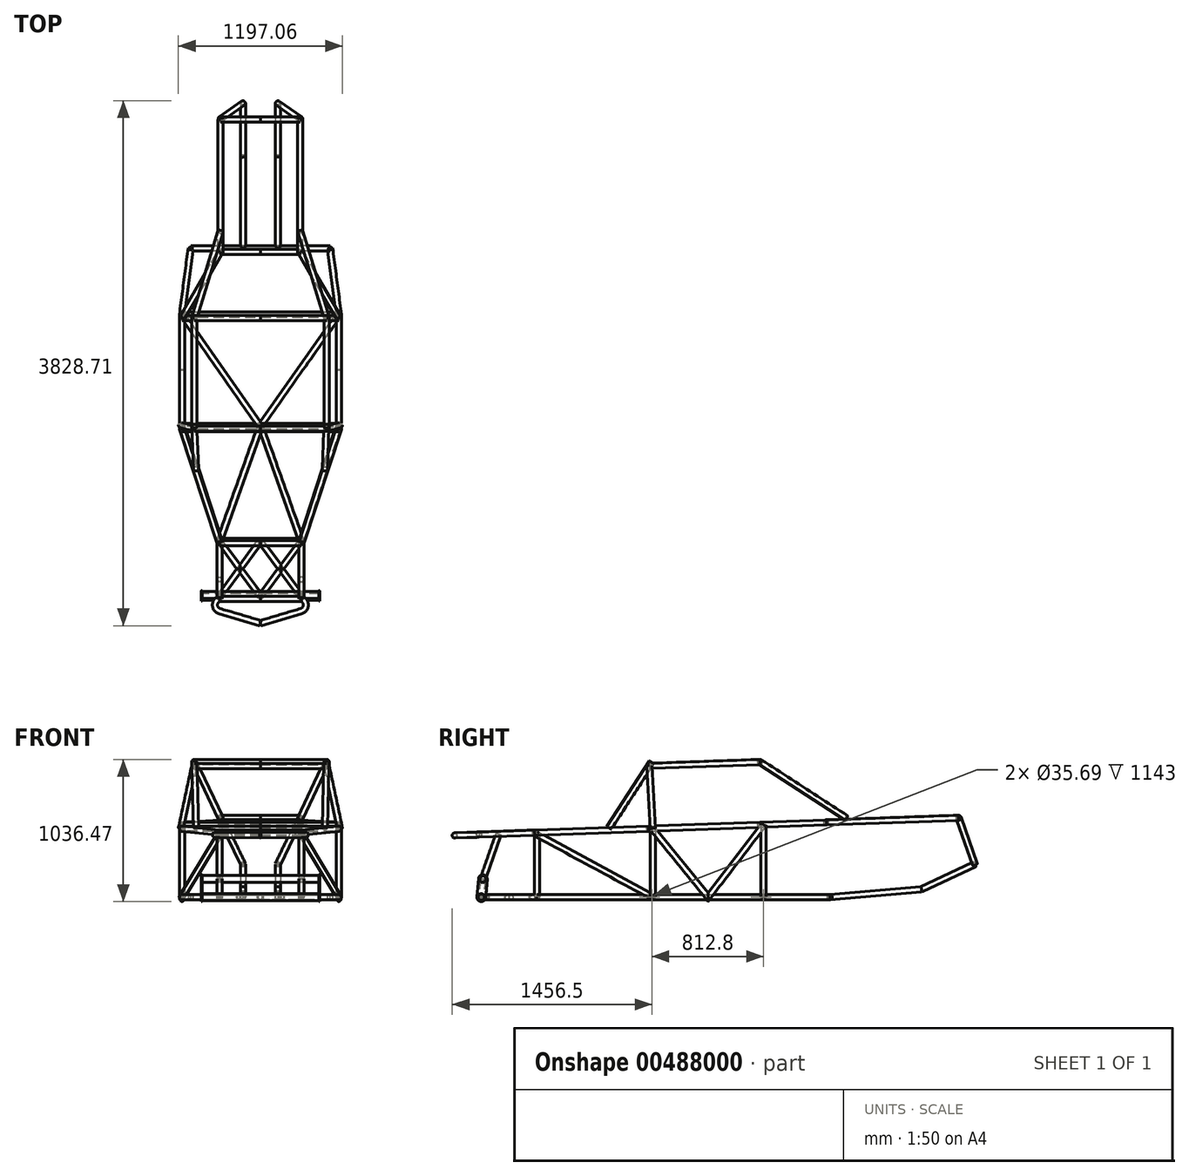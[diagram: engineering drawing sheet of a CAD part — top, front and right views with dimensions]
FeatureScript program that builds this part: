
annotation { "Feature Type Name" : "Feature", "Feature Type Description" : "" }
export const myFeature = defineFeature(function(context is Context, id is Id, definition is map)
    precondition{}
    {
        {
            var Q0;
            Q0=qCreatedBy(makeId("Top.planeOp"),FACE);
            var sketch = newSketch(context, id + "F0", { "sketchPlane" : qUnion([Q0])});
            skLineSegment(sketch, "E0", {"start": v(0, 0) * mm, "end": v(298.45, 0) * mm});
            skLineSegment(sketch, "E1", {"start": v(298.45, 0) * mm, "end": v(-298.45, 0) * mm});
            skLineSegment(sketch, "E2", {"start": v(-298.45, 0) * mm, "end": v(-298.45, 406.4) * mm});
            skLineSegment(sketch, "E3", {"start": v(298.45, 0) * mm, "end": v(298.45, 406.4) * mm});
            skLineSegment(sketch, "E4", {"start": v(-298.45, 406.4) * mm, "end": v(298.45, 406.4) * mm});
            skLineSegment(sketch, "E5", {"start": v(-571.5, 1244.6) * mm, "end": v(-298.45, 406.4) * mm});
            skLineSegment(sketch, "E6", {"start": v(298.45, 406.4) * mm, "end": v(571.5, 1244.6) * mm});
            skLineSegment(sketch, "E7", {"start": v(-571.5, 1244.6) * mm, "end": v(571.5, 1244.6) * mm});
            skLineSegment(sketch, "E8", {"start": v(-571.5, 1244.6) * mm, "end": v(-571.5, 2057.4) * mm});
            skLineSegment(sketch, "E9", {"start": v(571.5, 1244.6) * mm, "end": v(571.5, 2057.4) * mm});
            skLineSegment(sketch, "E10", {"start": v(508, 2540) * mm, "end": v(571.5, 2057.4) * mm});
            skLineSegment(sketch, "E11", {"start": v(-571.5, 2057.4) * mm, "end": v(-508, 2540) * mm});
            skLineSegment(sketch, "E12", {"start": v(-571.5, 2057.4) * mm, "end": v(571.5, 2057.4) * mm});
            skLineSegment(sketch, "E13", {"start": v(-508, 2540) * mm, "end": v(508, 2540) * mm});
            skLineSegment(sketch, "E14", {"start": v(0, 0) * mm, "end": v(0, 2540) * mm});
            skLineSegment(sketch, "E15", {"start": v(-298.45, 406.4) * mm, "end": v(0, 0) * mm});
            skLineSegment(sketch, "E16", {"start": v(0, 406.4) * mm, "end": v(-298.45, 0) * mm});
            skLineSegment(sketch, "E17", {"start": v(298.45, 0) * mm, "end": v(0, 406.4) * mm});
            skLineSegment(sketch, "E18", {"start": v(0, 0) * mm, "end": v(298.45, 406.4) * mm});
            skLineSegment(sketch, "E19", {"start": v(-298.45, 406.4) * mm, "end": v(0, 1244.6) * mm});
            skLineSegment(sketch, "E20", {"start": v(0, 1244.6) * mm, "end": v(298.45, 406.4) * mm});
            skLineSegment(sketch, "E21", {"start": v(0, 1244.6) * mm, "end": v(-571.5, 2057.4) * mm});
            skLineSegment(sketch, "E22", {"start": v(0, 1244.6) * mm, "end": v(571.5, 2057.4) * mm});
            skSolve(sketch);
        }
        {
            var Q0;
            Q0=qCreatedBy(makeId("Top.planeOp"),FACE);
            cPlane(context, id + "F1", {"entities" : qUnion([Q0]), "cplaneType" : CPlaneType.OFFSET, "offset" : 457.2 * mm, "width" : 152.4 * mm, "height" : 152.4 * mm});
        }
        {
            var Q0;
            Q0=qCreatedBy(id+"F1.planeOp",FACE);
            var sketch = newSketch(context, id + "F2", { "sketchPlane" : qUnion([Q0])});
            skLineSegment(sketch, "E23", {"start": v(0, 0) * mm, "end": v(298.45, 0) * mm});
            skLineSegment(sketch, "E24", {"start": v(298.45, 0) * mm, "end": v(298.45, 406.4) * mm});
            skLineSegment(sketch, "E25", {"start": v(298.45, 406.4) * mm, "end": v(571.34, 1239.13) * mm});
            skLineSegment(sketch, "E26", {"start": v(571.34, 1239.13) * mm, "end": v(571.34, 2051.93) * mm});
            skLineSegment(sketch, "E27", {"start": v(0, 0) * mm, "end": v(-298.45, 0) * mm});
            skLineSegment(sketch, "E28", {"start": v(-298.45, 0) * mm, "end": v(-298.45, 406.4) * mm});
            skLineSegment(sketch, "E29", {"start": v(-298.45, 406.4) * mm, "end": v(-570.8, 1239.3) * mm});
            skLineSegment(sketch, "E30", {"start": v(-570.8, 1239.3) * mm, "end": v(-570.8, 2052.1) * mm});
            skLineSegment(sketch, "E31", {"start": v(-298.45, 406.4) * mm, "end": v(298.45, 406.4) * mm});
            skLineSegment(sketch, "E32", {"start": v(571.34, 1239.13) * mm, "end": v(-570.8, 1239.3) * mm});
            skLineSegment(sketch, "E33", {"start": v(571.34, 2051.93) * mm, "end": v(-570.8, 2052.1) * mm});
            skLineSegment(sketch, "E34", {"start": v(310.25, 2534.7) * mm, "end": v(571.34, 2051.93) * mm});
            skLineSegment(sketch, "E35", {"start": v(-316.8, 2534.7) * mm, "end": v(-570.8, 2052.1) * mm});
            skLineSegment(sketch, "E36", {"start": v(-316.8, 2534.7) * mm, "end": v(310.25, 2534.7) * mm});
            skLineSegment(sketch, "E37", {"start": v(-316.8, 2534.7) * mm, "end": v(-316.8, 3499.9) * mm});
            skLineSegment(sketch, "E38", {"start": v(-316.8, 3499.9) * mm, "end": v(310.25, 3499.9) * mm});
            skLineSegment(sketch, "E39", {"start": v(310.25, 3499.9) * mm, "end": v(310.25, 2534.7) * mm});
            skLineSegment(sketch, "E40", {"start": v(-570.8, 1239.3) * mm, "end": v(298.45, 406.4) * mm});
            skLineSegment(sketch, "E41", {"start": v(571.34, 1239.13) * mm, "end": v(-298.45, 406.4) * mm});
            skSolve(sketch);
        }
        {
            var Q0;
            Q0=qCreatedBy(makeId("Front.planeOp"),FACE);
            var sketch = newSketch(context, id + "F3", { "sketchPlane" : qUnion([Q0])});
            skCircle(sketch, "E42", {"center": v(-298.45, 0) * mm, "radius": 19.05 * mm});
            skCircle(sketch, "E43", {"center": v(-298.45, 0) * mm, "radius": 17.84 * mm});
            skSolve(sketch);
        }
        {
            var Q0;
            Q0=makeQuery(id+"F3.imprint","IMPRINT",FACE,{"disambiguationData":[TD([[makeQuery(id+"F3.imprint","IMPRINT",EDGE,{"derivedFrom":sQuery(id+"F3.wireOp",EDGE,"E42")}),1.0]])]});
            var Q1;
            Q1=sQuery(id+"F0.wireOp",EDGE,"E2");
            var Q2;
            Q2=sQuery(id+"F0.wireOp",EDGE,"E5");
            var Q3;
            Q3=sQuery(id+"F0.wireOp",EDGE,"E8");
            var Q4;
            Q4=sQuery(id+"F0.wireOp",EDGE,"E11");
            sweep(context, id + "F4", {"profiles" : qUnion([Q0]), "path" : qUnion([Q1, Q2, Q3, Q4])});
        }
        {
            var Q0;
            Q0=sQuery(id+"F0.wireOp",EDGE,"E16");
            var Q1;
            Q1=sQuery(id+"F0.wireOp",VERTEX,"E16.end");
            cPlane(context, id + "F5", {"entities" : qUnion([Q0, Q1]), "cplaneType" : CPlaneType.LINE_POINT, "offset" : 25.4 * mm, "width" : 152.4 * mm, "height" : 152.4 * mm});
        }
        {
            var Q0;
            Q0=qCreatedBy(id+"F5.planeOp",FACE);
            var sketch = newSketch(context, id + "F6", { "sketchPlane" : qUnion([Q0])});
            skCircle(sketch, "E44", {"center": v(-240.55, 0) * mm, "radius": 19.05 * mm});
            skCircle(sketch, "E45", {"center": v(-240.55, 0) * mm, "radius": 17.84 * mm});
            skSolve(sketch);
        }
        {
            var Q0;
            Q0=makeQuery(id+"F6.imprint","IMPRINT",FACE,{"disambiguationData":[TD([[makeQuery(id+"F6.imprint","IMPRINT",EDGE,{"derivedFrom":sQuery(id+"F6.wireOp",EDGE,"E44")}),1.0]])]});
            var Q1;
            Q1=sQuery(id+"F0.wireOp",EDGE,"E16");
            sweep(context, id + "F7", {"operationType" : NewBodyOperationType.ADD, "profiles" : qUnion([Q0]), "path" : qUnion([Q1])});
        }
        {
            var Q0;
            Q0=sQuery(id+"F0.wireOp",VERTEX,"E15.end");
            var Q1;
            Q1=sQuery(id+"F0.wireOp",EDGE,"E15");
            cPlane(context, id + "F8", {"entities" : qUnion([Q0, Q1]), "cplaneType" : CPlaneType.LINE_POINT, "offset" : 25.4 * mm, "width" : 152.4 * mm, "height" : 152.4 * mm});
        }
        {
            var Q0;
            Q0=qCreatedBy(id+"F8.planeOp",FACE);
            var sketch = newSketch(context, id + "F9", { "sketchPlane" : qUnion([Q0])});
            skCircle(sketch, "E46", {"center": v(0, 0) * mm, "radius": 19.05 * mm});
            skCircle(sketch, "E47", {"center": v(0, 0) * mm, "radius": 17.84 * mm});
            skSolve(sketch);
        }
        {
            var Q0;
            Q0=makeQuery(id+"F9.imprint","IMPRINT",FACE,{"disambiguationData":[TD([[makeQuery(id+"F9.imprint","IMPRINT",EDGE,{"derivedFrom":sQuery(id+"F9.wireOp",EDGE,"E46")}),1.0]])]});
            var Q1;
            Q1=sQuery(id+"F0.wireOp",EDGE,"E15");
            sweep(context, id + "F10", {"operationType" : NewBodyOperationType.ADD, "profiles" : qUnion([Q0]), "path" : qUnion([Q1])});
        }
        {
            var Q0;
            Q0=makeQuery(id+"F4.opSweep","SWEPT_BODY",BODY,{"disambiguationData":[OSD([sQuery(id+"F0.wireOp",EDGE,"E11"),sQuery(id+"F3.wireOp",EDGE,"E42"),sQuery(id+"F3.wireOp",EDGE,"E43")])]});
            var Q1;
            Q1=qCreatedBy(makeId("Right.planeOp"),FACE);
            mirror(context, id + "F11", {"entities" : qUnion([Q0]), "mirrorPlane" : qUnion([Q1])});
        }
        {
            var Q0;
            Q0=sQuery(id+"F0.wireOp",VERTEX,"E19.start");
            var Q1;
            Q1=sQuery(id+"F0.wireOp",EDGE,"E4");
            cPlane(context, id + "F12", {"entities" : qUnion([Q0, Q1]), "cplaneType" : CPlaneType.LINE_POINT, "offset" : 25.4 * mm, "width" : 152.4 * mm, "height" : 152.4 * mm});
        }
        {
            var Q0;
            Q0=qCreatedBy(id+"F12.planeOp",FACE);
            var sketch = newSketch(context, id + "F13", { "sketchPlane" : qUnion([Q0])});
            skCircle(sketch, "E48", {"center": v(406.4, 0) * mm, "radius": 19.05 * mm});
            skCircle(sketch, "E49", {"center": v(406.4, 0) * mm, "radius": 17.84 * mm});
            skSolve(sketch);
        }
        {
            var Q0;
            Q0 = qSketchRegion(id + "F13", true);
            var Q1;
            Q1=sQuery(id+"F0.wireOp",EDGE,"E4");
            sweep(context, id + "F14", {"profiles" : qUnion([Q0]), "path" : qUnion([Q1])});
        }
        {
            var Q0;
            Q0=sQuery(id+"F0.wireOp",VERTEX,"E5.start");
            var Q1;
            Q1=sQuery(id+"F0.wireOp",EDGE,"E7");
            cPlane(context, id + "F15", {"entities" : qUnion([Q0, Q1]), "cplaneType" : CPlaneType.LINE_POINT, "offset" : 25.4 * mm, "width" : 152.4 * mm, "height" : 152.4 * mm});
        }
        {
            var Q0;
            Q0=qCreatedBy(id+"F15.planeOp",FACE);
            var sketch = newSketch(context, id + "F16", { "sketchPlane" : qUnion([Q0])});
            skCircle(sketch, "E50", {"center": v(1244.6, 0) * mm, "radius": 19.05 * mm});
            skCircle(sketch, "E51", {"center": v(1244.6, 0) * mm, "radius": 17.84 * mm});
            skCircle(sketch, "E52", {"center": v(2057.4, 0) * mm, "radius": 19.05 * mm});
            skCircle(sketch, "E53", {"center": v(2057.4, 0) * mm, "radius": 17.84 * mm});
            skSolve(sketch);
        }
        {
            var Q0;
            Q0 = qSketchRegion(id + "F16", true);
            var Q1;
            Q1=sQuery(id+"F0.wireOp",EDGE,"E7");
            sweep(context, id + "F17", {"profiles" : qUnion([Q0]), "path" : qUnion([Q1])});
        }
        {
            var Q0;
            Q0=sQuery(id+"F0.wireOp",VERTEX,"E11.end");
            var Q1;
            Q1=sQuery(id+"F0.wireOp",EDGE,"E13");
            cPlane(context, id + "F18", {"entities" : qUnion([Q0, Q1]), "cplaneType" : CPlaneType.LINE_POINT, "offset" : 25.4 * mm, "width" : 152.4 * mm, "height" : 152.4 * mm});
        }
        {
            var Q0;
            Q0=qCreatedBy(id+"F18.planeOp",FACE);
            var sketch = newSketch(context, id + "F19", { "sketchPlane" : qUnion([Q0])});
            skCircle(sketch, "E54", {"center": v(2540, 0) * mm, "radius": 19.05 * mm});
            skCircle(sketch, "E55", {"center": v(2540, 0) * mm, "radius": 17.84 * mm});
            skSolve(sketch);
        }
        {
            var Q0;
            Q0 = qSketchRegion(id + "F19", true);
            var Q1;
            Q1=sQuery(id+"F0.wireOp",EDGE,"E13");
            sweep(context, id + "F20", {"profiles" : qUnion([Q0]), "path" : qUnion([Q1])});
        }
        {
            var Q0;
            Q0=sQuery(id+"F0.wireOp",VERTEX,"E19.start");
            var Q1;
            Q1=sQuery(id+"F0.wireOp",EDGE,"E19");
            cPlane(context, id + "F21", {"entities" : qUnion([Q0, Q1]), "cplaneType" : CPlaneType.LINE_POINT, "offset" : 25.4 * mm, "width" : 152.4 * mm, "height" : 152.4 * mm});
        }
        {
            var Q0;
            Q0=qCreatedBy(id+"F21.planeOp",FACE);
            var sketch = newSketch(context, id + "F22", { "sketchPlane" : qUnion([Q0])});
            skCircle(sketch, "E56", {"center": v(417.48, 0) * mm, "radius": 19.05 * mm});
            skCircle(sketch, "E57", {"center": v(417.48, 0) * mm, "radius": 17.84 * mm});
            skSolve(sketch);
        }
        {
            var Q0;
            Q0 = qSketchRegion(id + "F22", true);
            var Q1;
            Q1=sQuery(id+"F0.wireOp",EDGE,"E19");
            var Q2;
            Q2=sQuery(id+"F0.wireOp",EDGE,"E21");
            sweep(context, id + "F23", {"profiles" : qUnion([Q0]), "path" : qUnion([Q1, Q2])});
        }
        {
            var Q0;
            Q0=makeQuery(id+"F23.opSweep","SWEPT_BODY",BODY,{"disambiguationData":[OSD([sQuery(id+"F0.wireOp",EDGE,"E21"),sQuery(id+"F22.wireOp",EDGE,"E56"),sQuery(id+"F22.wireOp",EDGE,"E57")])]});
            var Q1;
            Q1=qCreatedBy(makeId("Right.planeOp"),FACE);
            mirror(context, id + "F24", {"entities" : qUnion([Q0]), "mirrorPlane" : qUnion([Q1])});
        }
        {
            var Q0;
            Q0=qCreatedBy(id+"F1.planeOp",FACE);
            var Q1;
            Q1=sQuery(id+"F2.wireOp",EDGE,"E27");
            cPlane(context, id + "F25", {"entities" : qUnion([Q0, Q1]), "cplaneType" : CPlaneType.LINE_ANGLE, "offset" : 25.4 * mm, "angle" : 178 * degree, "width" : 152.4 * mm, "height" : 152.4 * mm});
        }
        {
            var Q0;
            Q0=qCreatedBy(id+"F25.planeOp",FACE);
            var sketch = newSketch(context, id + "F26", { "sketchPlane" : qUnion([Q0])});
            skLineSegment(sketch, "E58", {"start": v(0, 0) * mm, "end": v(298.45, 0) * mm});
            skLineSegment(sketch, "E59", {"start": v(298.45, 0) * mm, "end": v(298.45, 407.92) * mm});
            skLineSegment(sketch, "E60", {"start": v(571.5, 1239.87) * mm, "end": v(298.45, 407.92) * mm});
            skLineSegment(sketch, "E61", {"start": v(571.5, 1239.87) * mm, "end": v(571.5, 2049.6) * mm});
            skLineSegment(sketch, "E62", {"start": v(298.45, 407.92) * mm, "end": v(0, 407.92) * mm});
            skLineSegment(sketch, "E63", {"start": v(571.5, 1239.87) * mm, "end": v(0, 1239.87) * mm});
            skLineSegment(sketch, "E64", {"start": v(571.5, 2049.6) * mm, "end": v(0, 2049.6) * mm});
            skLineSegment(sketch, "E65", {"start": v(291.24, 2531.52) * mm, "end": v(571.5, 2049.6) * mm});
            skLineSegment(sketch, "E66", {"start": v(291.24, 2531.52) * mm, "end": v(291.24, 3496.72) * mm});
            skLineSegment(sketch, "E67", {"start": v(291.24, 2531.52) * mm, "end": v(0, 2531.52) * mm});
            skLineSegment(sketch, "E68", {"start": v(291.24, 3496.72) * mm, "end": v(0, 3496.72) * mm});
            skSolve(sketch);
        }
        {
            var Q0;
            Q0=sQuery(id+"F26.wireOp",VERTEX,"E58.start");
            var Q1;
            Q1=sQuery(id+"F26.wireOp",EDGE,"E58");
            cPlane(context, id + "F27", {"entities" : qUnion([Q0, Q1]), "cplaneType" : CPlaneType.LINE_POINT, "offset" : 25.4 * mm, "width" : 152.4 * mm, "height" : 152.4 * mm});
        }
        {
            var Q0;
            Q0=qCreatedBy(id+"F27.planeOp",FACE);
            var sketch = newSketch(context, id + "F28", { "sketchPlane" : qUnion([Q0])});
            skCircle(sketch, "E69", {"center": v(-15.95, 456.64) * mm, "radius": 19.05 * mm});
            skCircle(sketch, "E70", {"center": v(-15.95, 456.64) * mm, "radius": 17.84 * mm});
            skCircle(sketch, "E71", {"center": v(391.73, 470.88) * mm, "radius": 19.05 * mm});
            skCircle(sketch, "E72", {"center": v(391.73, 470.88) * mm, "radius": 17.84 * mm});
            skSolve(sketch);
        }
        {
            var Q0;
            Q0 = qSketchRegion(id + "F28", true);
            var Q1;
            Q1=sQuery(id+"F26.wireOp",EDGE,"E58");
            sweep(context, id + "F29", {"profiles" : qUnion([Q0]), "path" : qUnion([Q1])});
        }
        {
            var Q0;
            Q0=sQuery(id+"F26.wireOp",VERTEX,"E63.end");
            var Q1;
            Q1=sQuery(id+"F26.wireOp",EDGE,"E63");
            cPlane(context, id + "F30", {"entities" : qUnion([Q0, Q1]), "cplaneType" : CPlaneType.LINE_POINT, "offset" : 25.4 * mm, "width" : 152.4 * mm, "height" : 152.4 * mm});
        }
        {
            var Q0;
            Q0=qCreatedBy(id+"F30.planeOp",FACE);
            var sketch = newSketch(context, id + "F31", { "sketchPlane" : qUnion([Q0])});
            skCircle(sketch, "E73", {"center": v(-1223.17, 499.91) * mm, "radius": 19.05 * mm});
            skCircle(sketch, "E74", {"center": v(-1223.17, 499.91) * mm, "radius": 17.84 * mm});
            skCircle(sketch, "E75", {"center": v(-2032.4, 528.17) * mm, "radius": 19.05 * mm});
            skCircle(sketch, "E76", {"center": v(-2032.4, 528.17) * mm, "radius": 17.84 * mm});
            skSolve(sketch);
        }
        {
            var Q0;
            Q0 = qSketchRegion(id + "F31", true);
            var Q1;
            Q1=sQuery(id+"F26.wireOp",EDGE,"E63");
            sweep(context, id + "F32", {"profiles" : qUnion([Q0]), "path" : qUnion([Q1])});
        }
        {
            var Q0;
            Q0=sQuery(id+"F26.wireOp",VERTEX,"E67.end");
            var Q1;
            Q1=sQuery(id+"F26.wireOp",EDGE,"E67");
            cPlane(context, id + "F33", {"entities" : qUnion([Q0, Q1]), "cplaneType" : CPlaneType.LINE_POINT, "offset" : 25.4 * mm, "width" : 152.4 * mm, "height" : 152.4 * mm});
        }
        {
            var Q0;
            Q0=qCreatedBy(id+"F33.planeOp",FACE);
            var sketch = newSketch(context, id + "F34", { "sketchPlane" : qUnion([Q0])});
            skCircle(sketch, "E77", {"center": v(-2514.04, 545) * mm, "radius": 19.05 * mm});
            skCircle(sketch, "E78", {"center": v(-2514.04, 545) * mm, "radius": 17.84 * mm});
            skCircle(sketch, "E79", {"center": v(-3478.65, 578.68) * mm, "radius": 19.05 * mm});
            skCircle(sketch, "E80", {"center": v(-3478.65, 578.68) * mm, "radius": 17.84 * mm});
            skSolve(sketch);
        }
        {
            var Q0;
            Q0 = qSketchRegion(id + "F34", true);
            var Q1;
            Q1=sQuery(id+"F26.wireOp",EDGE,"E67");
            sweep(context, id + "F35", {"profiles" : qUnion([Q0]), "path" : qUnion([Q1])});
        }
        {
            var Q0;
            Q0=sQuery(id+"F26.wireOp",VERTEX,"E59.start");
            var Q1;
            Q1=sQuery(id+"F26.wireOp",EDGE,"E59");
            cPlane(context, id + "F36", {"entities" : qUnion([Q0, Q1]), "cplaneType" : CPlaneType.LINE_POINT, "offset" : 25.4 * mm, "width" : 152.4 * mm, "height" : 152.4 * mm});
        }
        {
            var Q0;
            Q0=qCreatedBy(id+"F36.planeOp",FACE);
            var sketch = newSketch(context, id + "F37", { "sketchPlane" : qUnion([Q0])});
            skCircle(sketch, "E81", {"center": v(-298.45, 456.92) * mm, "radius": 19.05 * mm});
            skCircle(sketch, "E82", {"center": v(-298.45, 456.92) * mm, "radius": 17.84 * mm});
            skSolve(sketch);
        }
        {
            var Q0;
            Q0 = qSketchRegion(id + "F37", true);
            var Q1;
            Q1=sQuery(id+"F26.wireOp",EDGE,"E59");
            var Q2;
            Q2=sQuery(id+"F26.wireOp",EDGE,"E60");
            var Q3;
            Q3=sQuery(id+"F26.wireOp",EDGE,"E61");
            var Q4;
            Q4=sQuery(id+"F26.wireOp",EDGE,"E65");
            var Q5;
            Q5=sQuery(id+"F26.wireOp",EDGE,"E66");
            sweep(context, id + "F38", {"profiles" : qUnion([Q0]), "path" : qUnion([Q1, Q2, Q3, Q4, Q5])});
        }
        {
            var Q0;
            Q0=makeQuery(id+"F29.opSweep","SWEPT_BODY",BODY,{"disambiguationData":[OSD([sQuery(id+"F26.wireOp",EDGE,"E58"),sQuery(id+"F28.wireOp",EDGE,"E69"),sQuery(id+"F28.wireOp",EDGE,"E70")])]});
            var Q1;
            Q1=makeQuery(id+"F29.opSweep","SWEPT_BODY",BODY,{"disambiguationData":[OSD([sQuery(id+"F26.wireOp",EDGE,"E58"),sQuery(id+"F28.wireOp",EDGE,"E71"),sQuery(id+"F28.wireOp",EDGE,"E72")])]});
            var Q2;
            Q2=makeQuery(id+"F32.opSweep","SWEPT_BODY",BODY,{"disambiguationData":[OSD([sQuery(id+"F26.wireOp",EDGE,"E63"),sQuery(id+"F31.wireOp",EDGE,"E73"),sQuery(id+"F31.wireOp",EDGE,"E74")])]});
            var Q3;
            Q3=makeQuery(id+"F32.opSweep","SWEPT_BODY",BODY,{"disambiguationData":[OSD([sQuery(id+"F26.wireOp",EDGE,"E63"),sQuery(id+"F31.wireOp",EDGE,"E75"),sQuery(id+"F31.wireOp",EDGE,"E76")])]});
            var Q4;
            Q4=makeQuery(id+"F35.opSweep","SWEPT_BODY",BODY,{"disambiguationData":[OSD([sQuery(id+"F26.wireOp",EDGE,"E67"),sQuery(id+"F34.wireOp",EDGE,"E77"),sQuery(id+"F34.wireOp",EDGE,"E78")])]});
            var Q5;
            Q5=makeQuery(id+"F35.opSweep","SWEPT_BODY",BODY,{"disambiguationData":[OSD([sQuery(id+"F26.wireOp",EDGE,"E67"),sQuery(id+"F34.wireOp",EDGE,"E79"),sQuery(id+"F34.wireOp",EDGE,"E80")])]});
            var Q6;
            Q6=makeQuery(id+"F38.opSweep","SWEPT_BODY",BODY,{"disambiguationData":[OSD([sQuery(id+"F26.wireOp",EDGE,"E66"),sQuery(id+"F37.wireOp",EDGE,"E81"),sQuery(id+"F37.wireOp",EDGE,"E82")])]});
            var Q7;
            Q7=qCreatedBy(id+"F27.planeOp",FACE);
            mirror(context, id + "F39", {"entities" : qUnion([Q0, Q1, Q2, Q3, Q4, Q5, Q6]), "mirrorPlane" : qUnion([Q7])});
        }
        {
            var Q0;
            Q0=qCreatedBy(id+"F15.planeOp",FACE);
            var sketch = newSketch(context, id + "F40", { "sketchPlane" : qUnion([Q0])});
            skLineSegment(sketch, "E83", {"start": v(1251.69, 0) * mm, "end": v(1251.69, 499.7) * mm});
            skLineSegment(sketch, "E84", {"start": v(2058.56, 0) * mm, "end": v(2058.56, 528.86) * mm});
            skSolve(sketch);
        }
        {
            var Q0;
            Q0=sQuery(id+"F40.wireOp",EDGE,"E84");
            var Q1;
            Q1=sQuery(id+"F40.wireOp",VERTEX,"E84.end");
            cPlane(context, id + "F41", {"entities" : qUnion([Q0, Q1]), "cplaneType" : CPlaneType.LINE_POINT, "offset" : 25.4 * mm, "width" : 152.4 * mm, "height" : 152.4 * mm});
        }
        {
            var Q0;
            Q0=qCreatedBy(id+"F41.planeOp",FACE);
            var sketch = newSketch(context, id + "F42", { "sketchPlane" : qUnion([Q0])});
            skCircle(sketch, "E85", {"center": v(-571.5, 2058.56) * mm, "radius": 19.05 * mm});
            skCircle(sketch, "E86", {"center": v(-571.5, 2058.56) * mm, "radius": 17.84 * mm});
            skSolve(sketch);
        }
        {
            var Q0;
            Q0 = qSketchRegion(id + "F42", true);
            var Q1;
            Q1=sQuery(id+"F40.wireOp",EDGE,"E84");
            sweep(context, id + "F43", {"profiles" : qUnion([Q0]), "path" : qUnion([Q1])});
        }
        {
            var Q0;
            Q0=sQuery(id+"F40.wireOp",VERTEX,"E83.end");
            var Q1;
            Q1=sQuery(id+"F40.wireOp",EDGE,"E83");
            cPlane(context, id + "F44", {"entities" : qUnion([Q0, Q1]), "cplaneType" : CPlaneType.LINE_POINT, "offset" : 25.4 * mm, "width" : 152.4 * mm, "height" : 152.4 * mm});
        }
        {
            var Q0;
            Q0=qCreatedBy(id+"F44.planeOp",FACE);
            var sketch = newSketch(context, id + "F45", { "sketchPlane" : qUnion([Q0])});
            skCircle(sketch, "E87", {"center": v(-571.5, 1251.69) * mm, "radius": 19.05 * mm});
            skCircle(sketch, "E88", {"center": v(-571.5, 1251.69) * mm, "radius": 17.84 * mm});
            skSolve(sketch);
        }
        {
            var Q0;
            Q0 = qSketchRegion(id + "F45", true);
            var Q1;
            Q1=sQuery(id+"F40.wireOp",EDGE,"E83");
            sweep(context, id + "F46", {"profiles" : qUnion([Q0]), "path" : qUnion([Q1])});
        }
        {
            var Q0;
            Q0=qCreatedBy(id+"F12.planeOp",FACE);
            var sketch = newSketch(context, id + "F47", { "sketchPlane" : qUnion([Q0])});
            skLineSegment(sketch, "E89", {"start": v(407.7, 0) * mm, "end": v(407.7, 467.6) * mm});
            skSolve(sketch);
        }
        {
            var Q0;
            Q0=sQuery(id+"F47.wireOp",VERTEX,"E89.end");
            var Q1;
            Q1=sQuery(id+"F47.wireOp",EDGE,"E89");
            cPlane(context, id + "F48", {"entities" : qUnion([Q0, Q1]), "cplaneType" : CPlaneType.LINE_POINT, "offset" : 25.4 * mm, "width" : 152.4 * mm, "height" : 152.4 * mm});
        }
        {
            var Q0;
            Q0=qCreatedBy(id+"F48.planeOp",FACE);
            var sketch = newSketch(context, id + "F49", { "sketchPlane" : qUnion([Q0])});
            skCircle(sketch, "E90", {"center": v(-298.45, 407.7) * mm, "radius": 19.05 * mm});
            skCircle(sketch, "E91", {"center": v(-298.45, 407.7) * mm, "radius": 17.84 * mm});
            skSolve(sketch);
        }
        {
            var Q0;
            Q0 = qSketchRegion(id + "F49", true);
            var Q1;
            Q1=sQuery(id+"F47.wireOp",EDGE,"E89");
            sweep(context, id + "F50", {"profiles" : qUnion([Q0]), "path" : qUnion([Q1])});
        }
        {
            var Q0;
            Q0=makeQuery(id+"F43.opSweep","SWEPT_BODY",BODY,{"disambiguationData":[OSD([sQuery(id+"F40.wireOp",EDGE,"E84"),sQuery(id+"F42.wireOp",EDGE,"E85"),sQuery(id+"F42.wireOp",EDGE,"E86")])]});
            var Q1;
            Q1=makeQuery(id+"F46.opSweep","SWEPT_BODY",BODY,{"disambiguationData":[OSD([sQuery(id+"F40.wireOp",EDGE,"E83"),sQuery(id+"F45.wireOp",EDGE,"E87"),sQuery(id+"F45.wireOp",EDGE,"E88")])]});
            var Q2;
            Q2=makeQuery(id+"F50.opSweep","SWEPT_BODY",BODY,{"disambiguationData":[OSD([sQuery(id+"F47.wireOp",EDGE,"E89"),sQuery(id+"F49.wireOp",EDGE,"E90"),sQuery(id+"F49.wireOp",EDGE,"E91")])]});
            var Q3;
            Q3=qCreatedBy(makeId("Right.planeOp"),FACE);
            mirror(context, id + "F51", {"entities" : qUnion([Q0, Q1, Q2]), "mirrorPlane" : qUnion([Q3])});
        }
        {
            var Q0;
            Q0=qCreatedBy(id+"F25.planeOp",FACE);
            cPlane(context, id + "F52", {"entities" : qUnion([Q0]), "cplaneType" : CPlaneType.OFFSET, "offset" : 457.2 * mm, "width" : 152.4 * mm, "height" : 152.4 * mm});
        }
        {
            var Q0;
            Q0=qCreatedBy(id+"F52.planeOp",FACE);
            var sketch = newSketch(context, id + "F53", { "sketchPlane" : qUnion([Q0])});
            skLineSegment(sketch, "E92", {"start": v(0, 1257.74) * mm, "end": v(482.6, 1257.74) * mm});
            skLineSegment(sketch, "E93", {"start": v(482.6, 1257.74) * mm, "end": v(482.6, 2066.05) * mm});
            skLineSegment(sketch, "E94", {"start": v(482.6, 2066.05) * mm, "end": v(0, 2066.05) * mm});
            skSolve(sketch);
        }
        {
            var Q0;
            Q0=sQuery(id+"F53.wireOp",VERTEX,"E94.end");
            var Q1;
            Q1=sQuery(id+"F53.wireOp",EDGE,"E94");
            cPlane(context, id + "F54", {"entities" : qUnion([Q0, Q1]), "cplaneType" : CPlaneType.LINE_POINT, "offset" : 25.4 * mm, "width" : 152.4 * mm, "height" : 152.4 * mm});
        }
        {
            var Q0;
            Q0=qCreatedBy(id+"F54.planeOp",FACE);
            var sketch = newSketch(context, id + "F55", { "sketchPlane" : qUnion([Q0])});
            skCircle(sketch, "E95", {"center": v(-2032.89, 985.67) * mm, "radius": 19.05 * mm});
            skCircle(sketch, "E96", {"center": v(-2032.89, 985.67) * mm, "radius": 17.84 * mm});
            skCircle(sketch, "E97", {"center": v(-1225.07, 957.46) * mm, "radius": 19.05 * mm});
            skCircle(sketch, "E98", {"center": v(-1225.07, 957.46) * mm, "radius": 17.84 * mm});
            skSolve(sketch);
        }
        {
            var Q0;
            Q0 = qSketchRegion(id + "F55", true);
            var Q1;
            Q1=sQuery(id+"F53.wireOp",EDGE,"E92");
            sweep(context, id + "F56", {"profiles" : qUnion([Q0]), "path" : qUnion([Q1])});
        }
        {
            var Q0;
            Q0=sQuery(id+"F53.wireOp",VERTEX,"E93.start");
            var Q1;
            Q1=sQuery(id+"F53.wireOp",EDGE,"E93");
            cPlane(context, id + "F57", {"entities" : qUnion([Q0, Q1]), "cplaneType" : CPlaneType.LINE_POINT, "offset" : 25.4 * mm, "width" : 152.4 * mm, "height" : 152.4 * mm});
        }
        {
            var Q0;
            Q0=qCreatedBy(id+"F57.planeOp",FACE);
            var sketch = newSketch(context, id + "F58", { "sketchPlane" : qUnion([Q0])});
            skCircle(sketch, "E99", {"center": v(-482.6, 914.12) * mm, "radius": 19.05 * mm});
            skCircle(sketch, "E100", {"center": v(-482.6, 914.12) * mm, "radius": 17.84 * mm});
            skSolve(sketch);
        }
        {
            var Q0;
            Q0 = qSketchRegion(id + "F58", true);
            var Q1;
            Q1=sQuery(id+"F53.wireOp",EDGE,"E93");
            sweep(context, id + "F59", {"profiles" : qUnion([Q0]), "path" : qUnion([Q1])});
        }
        {
            var Q0;
            Q0=makeQuery(id+"F56.opSweep","SWEPT_BODY",BODY,{"disambiguationData":[OSD([sQuery(id+"F53.wireOp",EDGE,"E92"),sQuery(id+"F55.wireOp",EDGE,"E97"),sQuery(id+"F55.wireOp",EDGE,"E98")])]});
            var Q1;
            Q1=makeQuery(id+"F59.opSweep","SWEPT_BODY",BODY,{"disambiguationData":[OSD([sQuery(id+"F53.wireOp",EDGE,"E93"),sQuery(id+"F58.wireOp",EDGE,"E99"),sQuery(id+"F58.wireOp",EDGE,"E100")])]});
            var Q2;
            Q2=makeQuery(id+"F56.opSweep","SWEPT_BODY",BODY,{"disambiguationData":[OSD([sQuery(id+"F53.wireOp",EDGE,"E92"),sQuery(id+"F55.wireOp",EDGE,"E95"),sQuery(id+"F55.wireOp",EDGE,"E96")])]});
            var Q3;
            Q3=qCreatedBy(id+"F54.planeOp",FACE);
            mirror(context, id + "F60", {"entities" : qUnion([Q0, Q1, Q2]), "mirrorPlane" : qUnion([Q3])});
        }
        {
            var Q0;
            Q0=qCreatedBy(id+"F52.planeOp",FACE);
            var Q1;
            Q1=makeQuery(id+"F60.opPattern","COPY",FACE,{"derivedFrom":makeQuery(id+"F59.opSweep","SWEPT_FACE",FACE,{"disambiguationData":[OSD([sQuery(id+"F53.wireOp",EDGE,"E93"),sQuery(id+"F58.wireOp",EDGE,"E99")])]}),"instanceName":"1"});
            cPlane(context, id + "F61", {"entities" : qUnion([Q0, Q1]), "cplaneType" : CPlaneType.LINE_ANGLE, "offset" : 25.4 * mm, "angle" : 98 * degree, "width" : 152.4 * mm, "height" : 152.4 * mm});
        }
        {
            var Q0;
            Q0=qCreatedBy(makeId("Top.planeOp"),FACE);
            var Q1;
            Q1=sQuery(id+"F0.wireOp",EDGE,"E1");
            cPlane(context, id + "F62", {"entities" : qUnion([Q0, Q1]), "cplaneType" : CPlaneType.LINE_ANGLE, "offset" : 25.4 * mm, "angle" : 95 * degree, "width" : 152.4 * mm, "height" : 152.4 * mm});
        }
        {
            var Q0;
            Q0=qCreatedBy(id+"F62.planeOp",FACE);
            var sketch = newSketch(context, id + "F63", { "sketchPlane" : qUnion([Q0])});
            skLineSegment(sketch, "E101", {"start": v(431.8, 133.35) * mm, "end": v(-431.8, 133.35) * mm});
            skLineSegment(sketch, "E102", {"start": v(298.45, 0) * mm, "end": v(298.45, 133.35) * mm});
            skLineSegment(sketch, "E103", {"start": v(-431.8, 0) * mm, "end": v(-298.45, 0) * mm});
            skLineSegment(sketch, "E104", {"start": v(-431.8, 0) * mm, "end": v(431.8, 0) * mm});
            skLineSegment(sketch, "E105", {"start": v(-298.45, 0) * mm, "end": v(-298.45, 133.35) * mm});
            skSolve(sketch);
        }
        {
            var Q0;
            Q0=sQuery(id+"F63.wireOp",VERTEX,"E101.start");
            var Q1;
            Q1=sQuery(id+"F63.wireOp",EDGE,"E101");
            cPlane(context, id + "F64", {"entities" : qUnion([Q0, Q1]), "cplaneType" : CPlaneType.LINE_POINT, "offset" : 25.4 * mm, "width" : 152.4 * mm, "height" : 152.4 * mm});
        }
        {
            var Q0;
            Q0=qCreatedBy(id+"F64.planeOp",FACE);
            var sketch = newSketch(context, id + "F65", { "sketchPlane" : qUnion([Q0])});
            skCircle(sketch, "E106", {"center": v(0, 0) * mm, "radius": 25.4 * mm});
            skCircle(sketch, "E107", {"center": v(0, 0) * mm, "radius": 22.35 * mm});
            skCircle(sketch, "E108", {"center": v(-11.62, 132.84) * mm, "radius": 25.4 * mm});
            skCircle(sketch, "E109", {"center": v(-11.62, 132.84) * mm, "radius": 22.35 * mm});
            skSolve(sketch);
        }
        {
            var Q0;
            Q0 = qSketchRegion(id + "F65", true);
            var Q1;
            Q1=sQuery(id+"F63.wireOp",EDGE,"E101");
            sweep(context, id + "F66", {"profiles" : qUnion([Q0]), "path" : qUnion([Q1])});
        }
        {
            var Q0;
            Q0=sQuery(id+"F63.wireOp",VERTEX,"E102.end");
            var Q1;
            Q1=sQuery(id+"F63.wireOp",EDGE,"E102");
            cPlane(context, id + "F67", {"entities" : qUnion([Q0, Q1]), "cplaneType" : CPlaneType.LINE_POINT, "offset" : 25.4 * mm, "width" : 152.4 * mm, "height" : 152.4 * mm});
        }
        {
            var Q0;
            Q0=qCreatedBy(id+"F67.planeOp",FACE);
            var sketch = newSketch(context, id + "F68", { "sketchPlane" : qUnion([Q0])});
            skCircle(sketch, "E110", {"center": v(298.45, 0) * mm, "radius": 19.05 * mm});
            skCircle(sketch, "E111", {"center": v(298.45, 0) * mm, "radius": 17.84 * mm});
            skSolve(sketch);
        }
        {
            var Q0;
            Q0 = qSketchRegion(id + "F68", true);
            var Q1;
            Q1=sQuery(id+"F63.wireOp",EDGE,"E102");
            sweep(context, id + "F69", {"profiles" : qUnion([Q0]), "path" : qUnion([Q1])});
        }
        {
            var Q0;
            Q0=makeQuery(id+"F69.opSweep","SWEPT_BODY",BODY,{"disambiguationData":[OSD([sQuery(id+"F63.wireOp",EDGE,"E102"),sQuery(id+"F68.wireOp",EDGE,"E110"),sQuery(id+"F68.wireOp",EDGE,"E111")])]});
            var Q1;
            Q1=qCreatedBy(makeId("Right.planeOp"),FACE);
            mirror(context, id + "F70", {"entities" : qUnion([Q0]), "mirrorPlane" : qUnion([Q1])});
        }
        {
            var Q0;
            Q0=qCreatedBy(id+"F64.planeOp",FACE);
            var sketch = newSketch(context, id + "F71", { "sketchPlane" : qUnion([Q0])});
            skArc(sketch, "E112", {"start": v(20, 135.6) * mm, "mid": v(-14.39, 164.47) * mm, "end": v(-43.25, 130.08) * mm});
            skArc(sketch, "E113", {"start": v(-31.63, -2.77) * mm, "mid": v(2.77, -31.63) * mm, "end": v(31.63, 2.77) * mm});
            skLineSegment(sketch, "E114", {"start": v(20, 135.6) * mm, "end": v(31.63, 2.77) * mm});
            skLineSegment(sketch, "E115", {"start": v(-43.25, 130.08) * mm, "end": v(-31.63, -2.77) * mm});
            skSolve(sketch);
        }
        {
            var Q0;
            Q0=makeQuery(id+"F71.imprint","IMPRINT",FACE,{"disambiguationData":[TD([[makeQuery(id+"F71.imprint","IMPRINT",EDGE,{"derivedFrom":sQuery(id+"F71.wireOp",EDGE,"E112")}),1.0]])]});
            var Q1;
            Q1=sQuery(id+"F71.wireOp",EDGE,"E112");
            var Q2;
            Q2=sQuery(id+"F71.wireOp",EDGE,"E114");
            var Q3;
            Q3=sQuery(id+"F71.wireOp",EDGE,"E113");
            var Q4;
            Q4=sQuery(id+"F71.wireOp",EDGE,"E115");
            extrude(context, id + "F72", {"entities" : qUnion([Q0]), "surfaceEntities" : qUnion([Q1, Q2, Q3, Q4]), "depth" : 6.35 * mm});
        }
        {
            var Q0;
            Q0=makeQuery(id+"F72.opExtrude","SWEPT_BODY",BODY,{"disambiguationData":[OSD([sQuery(id+"F71.wireOp",EDGE,"E112"),sQuery(id+"F71.wireOp",EDGE,"E113"),sQuery(id+"F71.wireOp",EDGE,"E114"),sQuery(id+"F71.wireOp",EDGE,"E115")])]});
            var Q1;
            Q1=qCreatedBy(makeId("Right.planeOp"),FACE);
            mirror(context, id + "F73", {"entities" : qUnion([Q0]), "mirrorPlane" : qUnion([Q1])});
        }
        {
            var Q0;
            Q0=qCreatedBy(id+"F25.planeOp",FACE);
            var sketch = newSketch(context, id + "F74", { "sketchPlane" : qUnion([Q0])});
            skLineSegment(sketch, "E116", {"start": v(0, 0) * mm, "end": v(0, -177.8) * mm});
            skLineSegment(sketch, "E117", {"start": v(0, -177.8) * mm, "end": v(298.45, -88.9) * mm});
            skArc(sketch, "E118", {"start": v(298.45, -88.9) * mm, "mid": v(331.55, -44.32) * mm, "end": v(298.1, 0) * mm});
            skSolve(sketch);
        }
        {
            var Q0;
            Q0=sQuery(id+"F74.wireOp",VERTEX,"E117.start");
            var Q1;
            Q1=sQuery(id+"F74.wireOp",EDGE,"E117");
            cPlane(context, id + "F75", {"entities" : qUnion([Q0, Q1]), "cplaneType" : CPlaneType.LINE_POINT, "offset" : 25.4 * mm, "width" : 152.4 * mm, "height" : 152.4 * mm});
        }
        {
            var Q0;
            Q0=qCreatedBy(id+"F75.planeOp",FACE);
            var sketch = newSketch(context, id + "F76", { "sketchPlane" : qUnion([Q0])});
            skCircle(sketch, "E119", {"center": v(-186.93, 450.41) * mm, "radius": 19.05 * mm});
            skCircle(sketch, "E120", {"center": v(-186.93, 450.41) * mm, "radius": 17.84 * mm});
            skSolve(sketch);
        }
        {
            var Q0;
            Q0 = qSketchRegion(id + "F76", true);
            var Q1;
            Q1=sQuery(id+"F74.wireOp",EDGE,"E117");
            var Q2;
            Q2=sQuery(id+"F74.wireOp",EDGE,"E118");
            sweep(context, id + "F77", {"profiles" : qUnion([Q0]), "path" : qUnion([Q1, Q2])});
        }
        {
            var Q0;
            Q0=makeQuery(id+"F77.opSweep","SWEPT_BODY",BODY,{"disambiguationData":[OSD([sQuery(id+"F74.wireOp",EDGE,"E118"),sQuery(id+"F76.wireOp",EDGE,"E119"),sQuery(id+"F76.wireOp",EDGE,"E120")])]});
            var Q1;
            Q1=qCreatedBy(makeId("Right.planeOp"),FACE);
            mirror(context, id + "F78", {"entities" : qUnion([Q0]), "mirrorPlane" : qUnion([Q1])});
        }
        {
            var Q0;
            Q0=sQuery(id+"F63.wireOp",VERTEX,"E102.end");
            var Q1;
            Q1=sQuery(id+"F63.wireOp",EDGE,"E101");
            cPlane(context, id + "F79", {"entities" : qUnion([Q0, Q1]), "cplaneType" : CPlaneType.LINE_POINT, "offset" : 25.4 * mm, "width" : 152.4 * mm, "height" : 152.4 * mm});
        }
        {
            var Q0;
            Q0=qCreatedBy(id+"F79.planeOp",FACE);
            var sketch = newSketch(context, id + "F80", { "sketchPlane" : qUnion([Q0])});
            skLineSegment(sketch, "E121", {"start": v(-11.17, 133.64) * mm, "end": v(-125.94, 461.32) * mm});
            skSolve(sketch);
        }
        {
            var Q0;
            Q0=sQuery(id+"F80.wireOp",VERTEX,"E121.end");
            var Q1;
            Q1=sQuery(id+"F80.wireOp",EDGE,"E121");
            cPlane(context, id + "F81", {"entities" : qUnion([Q0, Q1]), "cplaneType" : CPlaneType.LINE_POINT, "offset" : 25.4 * mm, "width" : 152.4 * mm, "height" : 152.4 * mm});
        }
        {
            var Q0;
            Q0=qCreatedBy(id+"F81.planeOp",FACE);
            var sketch = newSketch(context, id + "F82", { "sketchPlane" : qUnion([Q0])});
            skCircle(sketch, "E122", {"center": v(298.45, -33.64) * mm, "radius": 19.05 * mm});
            skCircle(sketch, "E123", {"center": v(298.45, -33.64) * mm, "radius": 17.84 * mm});
            skSolve(sketch);
        }
        {
            var Q0;
            Q0 = qSketchRegion(id + "F82", true);
            var Q1;
            Q1=sQuery(id+"F80.wireOp",EDGE,"E121");
            sweep(context, id + "F83", {"profiles" : qUnion([Q0]), "path" : qUnion([Q1])});
        }
        {
            var Q0;
            Q0=makeQuery(id+"F83.opSweep","SWEPT_BODY",BODY,{"disambiguationData":[OSD([sQuery(id+"F80.wireOp",EDGE,"E121"),sQuery(id+"F82.wireOp",EDGE,"E122"),sQuery(id+"F82.wireOp",EDGE,"E123")])]});
            var Q1;
            Q1=qCreatedBy(makeId("Right.planeOp"),FACE);
            mirror(context, id + "F84", {"entities" : qUnion([Q0]), "mirrorPlane" : qUnion([Q1])});
        }
        {
            var Q0;
            Q0=qCreatedBy(id+"F15.planeOp",FACE);
            var sketch = newSketch(context, id + "F85", { "sketchPlane" : qUnion([Q0])});
            skLineSegment(sketch, "E124", {"start": v(1654.01, 0) * mm, "end": v(2059.03, 528.32) * mm});
            skLineSegment(sketch, "E125", {"start": v(1654.01, 0) * mm, "end": v(1252.01, 496.33) * mm});
            skSolve(sketch);
        }
        {
            var Q0;
            Q0=sQuery(id+"F85.wireOp",VERTEX,"E124.end");
            var Q1;
            Q1=sQuery(id+"F85.wireOp",EDGE,"E124");
            cPlane(context, id + "F86", {"entities" : qUnion([Q0, Q1]), "cplaneType" : CPlaneType.LINE_POINT, "offset" : 25.4 * mm, "width" : 152.4 * mm, "height" : 152.4 * mm});
        }
        {
            var Q0;
            Q0=qCreatedBy(id+"F86.planeOp",FACE);
            var sketch = newSketch(context, id + "F87", { "sketchPlane" : qUnion([Q0])});
            skCircle(sketch, "E126", {"center": v(-571.5, 1312.67) * mm, "radius": 19.05 * mm});
            skCircle(sketch, "E127", {"center": v(-571.5, 1312.67) * mm, "radius": 17.84 * mm});
            skSolve(sketch);
        }
        {
            var Q0;
            Q0 = qSketchRegion(id + "F87", true);
            var Q1;
            Q1=sQuery(id+"F85.wireOp",EDGE,"E124");
            var Q2;
            Q2=sQuery(id+"F85.wireOp",EDGE,"E125");
            sweep(context, id + "F88", {"profiles" : qUnion([Q0]), "path" : qUnion([Q1, Q2])});
        }
        {
            var Q0;
            Q0=makeQuery(id+"F88.opSweep","SWEPT_BODY",BODY,{"disambiguationData":[OSD([sQuery(id+"F85.wireOp",EDGE,"E125"),sQuery(id+"F87.wireOp",EDGE,"E126"),sQuery(id+"F87.wireOp",EDGE,"E127")])]});
            var Q1;
            Q1=qCreatedBy(makeId("Right.planeOp"),FACE);
            mirror(context, id + "F89", {"entities" : qUnion([Q0]), "mirrorPlane" : qUnion([Q1])});
        }
        {
            var Q0;
            Q0=qCreatedBy(id+"F15.planeOp",FACE);
            var Q1;
            Q1=sQuery(id+"F40.wireOp",EDGE,"E83");
            cPlane(context, id + "F90", {"entities" : qUnion([Q0, Q1]), "cplaneType" : CPlaneType.LINE_ANGLE, "offset" : 25.4 * mm, "angle" : 18 * degree, "width" : 152.4 * mm, "height" : 152.4 * mm});
        }
        {
            var Q0;
            Q0=qCreatedBy(id+"F90.planeOp",FACE);
            var sketch = newSketch(context, id + "F91", { "sketchPlane" : qUnion([Q0])});
            skLineSegment(sketch, "E128", {"start": v(-1368.3, 0) * mm, "end": v(-480.93, 455.17) * mm});
            skSolve(sketch);
        }
        {
            var Q0;
            Q0=sQuery(id+"F91.wireOp",EDGE,"E128");
            var Q1;
            Q1=sQuery(id+"F91.wireOp",VERTEX,"E128.end");
            cPlane(context, id + "F92", {"entities" : qUnion([Q0, Q1]), "cplaneType" : CPlaneType.LINE_POINT, "offset" : 25.4 * mm, "width" : 152.4 * mm, "height" : 152.4 * mm});
        }
        {
            var Q0;
            Q0=qCreatedBy(id+"F92.planeOp",FACE);
            var sketch = newSketch(context, id + "F93", { "sketchPlane" : qUnion([Q0])});
            skCircle(sketch, "E129", {"center": v(-248.27, 595.32) * mm, "radius": 19.05 * mm});
            skCircle(sketch, "E130", {"center": v(-248.27, 595.32) * mm, "radius": 17.84 * mm});
            skSolve(sketch);
        }
        {
            var Q0;
            Q0 = qSketchRegion(id + "F93", true);
            var Q1;
            Q1=sQuery(id+"F91.wireOp",EDGE,"E128");
            sweep(context, id + "F94", {"profiles" : qUnion([Q0]), "path" : qUnion([Q1])});
        }
        {
            var Q0;
            Q0=makeQuery(id+"F94.opSweep","SWEPT_BODY",BODY,{"disambiguationData":[OSD([sQuery(id+"F91.wireOp",EDGE,"E128"),sQuery(id+"F93.wireOp",EDGE,"E129"),sQuery(id+"F93.wireOp",EDGE,"E130")])]});
            var Q1;
            Q1=qCreatedBy(makeId("Right.planeOp"),FACE);
            mirror(context, id + "F95", {"entities" : qUnion([Q0]), "mirrorPlane" : qUnion([Q1])});
        }
        {
            var Q0;
            Q0=sQuery(id+"F0.wireOp",VERTEX,"E14.end");
            var Q1;
            Q1=qCreatedBy(makeId("Top.planeOp"),FACE);
            cPlane(context, id + "F96", {"entities" : qUnion([Q0, Q1]), "cplaneType" : CPlaneType.PLANE_POINT, "offset" : 25.4 * mm, "width" : 152.4 * mm, "height" : 152.4 * mm});
        }
        {
            var Q0;
            Q0=qCreatedBy(id+"F96.planeOp",FACE);
            var Q1;
            Q1=sQuery(id+"F0.wireOp",EDGE,"E13");
            cPlane(context, id + "F97", {"entities" : qUnion([Q0, Q1]), "cplaneType" : CPlaneType.LINE_ANGLE, "offset" : 25.4 * mm, "angle" : 5 * degree, "width" : 152.4 * mm, "height" : 152.4 * mm});
        }
        {
            var Q0;
            Q0=qCreatedBy(id+"F97.planeOp",FACE);
            var sketch = newSketch(context, id + "F98", { "sketchPlane" : qUnion([Q0])});
            skLineSegment(sketch, "E131", {"start": v(-127, -3202.75) * mm, "end": v(-127, -2530.82) * mm});
            skLineSegment(sketch, "E132", {"start": v(127, -2530.82) * mm, "end": v(127, -3202.75) * mm});
            skLineSegment(sketch, "E133", {"start": v(127, -3202.75) * mm, "end": v(-127, -3202.75) * mm});
            skSolve(sketch);
        }
        {
            var Q0;
            Q0=sQuery(id+"F98.wireOp",VERTEX,"E133.end");
            var Q1;
            Q1=sQuery(id+"F98.wireOp",EDGE,"E131");
            cPlane(context, id + "F99", {"entities" : qUnion([Q0, Q1]), "cplaneType" : CPlaneType.LINE_POINT, "offset" : 25.4 * mm, "width" : 152.4 * mm, "height" : 152.4 * mm});
        }
        {
            var Q0;
            Q0=qCreatedBy(id+"F99.planeOp",FACE);
            var sketch = newSketch(context, id + "F100", { "sketchPlane" : qUnion([Q0])});
            skCircle(sketch, "E134", {"center": v(-127, -221.38) * mm, "radius": 19.05 * mm});
            skCircle(sketch, "E135", {"center": v(-127, -221.38) * mm, "radius": 17.84 * mm});
            skSolve(sketch);
        }
        {
            var Q0;
            Q0 = qSketchRegion(id + "F100", true);
            var Q1;
            Q1=sQuery(id+"F98.wireOp",EDGE,"E131");
            sweep(context, id + "F101", {"operationType" : NewBodyOperationType.ADD, "profiles" : qUnion([Q0]), "path" : qUnion([Q1])});
        }
        {
            var Q0;
            Q0=makeQuery(id+"F20.opSweep","SWEPT_BODY",BODY,{"disambiguationData":[OSD([sQuery(id+"F0.wireOp",EDGE,"E13"),sQuery(id+"F19.wireOp",EDGE,"E54"),sQuery(id+"F19.wireOp",EDGE,"E55")])]});
            var Q1;
            Q1=qCreatedBy(id+"F27.planeOp",FACE);
            mirror(context, id + "F102", {"entities" : qUnion([Q0]), "mirrorPlane" : qUnion([Q1])});
        }
        {
            var Q0;
            Q0=sQuery(id+"F98.wireOp",EDGE,"E133");
            cPoint(context, id + "F103", {"entities" : qUnion([Q0]), "parameter" : 0.5});
        }
        {
            var Q0;
            Q0=qCreatedBy(id+"F96.planeOp",FACE);
            var Q1;
            Q1 = qCreatedBy(id + "F103" ,VERTEX);
            cPlane(context, id + "F104", {"entities" : qUnion([Q0, Q1]), "cplaneType" : CPlaneType.PLANE_POINT, "offset" : 25.4 * mm, "width" : 152.4 * mm, "height" : 152.4 * mm});
        }
        {
            var Q0;
            Q0=qCreatedBy(id+"F104.planeOp",FACE);
            var Q1;
            Q1=sQuery(id+"F98.wireOp",EDGE,"E133");
            cPlane(context, id + "F105", {"entities" : qUnion([Q0, Q1]), "cplaneType" : CPlaneType.LINE_ANGLE, "offset" : 25.4 * mm, "angle" : 155 * degree, "width" : 152.4 * mm, "height" : 152.4 * mm});
        }
        {
            var Q0;
            Q0=qCreatedBy(id+"F105.planeOp",FACE);
            var sketch = newSketch(context, id + "F106", { "sketchPlane" : qUnion([Q0])});
            skLineSegment(sketch, "E136", {"start": v(126.7, 2934.22) * mm, "end": v(126.7, 3362.96) * mm});
            skLineSegment(sketch, "E137", {"start": v(126.7, 3362.96) * mm, "end": v(-127.65, 3362.96) * mm});
            skLineSegment(sketch, "E138", {"start": v(-127.65, 2934.65) * mm, "end": v(-127.65, 3362.96) * mm});
            skSolve(sketch);
        }
        {
            var Q0;
            Q0=sQuery(id+"F106.wireOp",VERTEX,"E137.start");
            var Q1;
            Q1=sQuery(id+"F106.wireOp",EDGE,"E136");
            cPlane(context, id + "F107", {"entities" : qUnion([Q0, Q1]), "cplaneType" : CPlaneType.LINE_POINT, "offset" : 25.4 * mm, "width" : 152.4 * mm, "height" : 152.4 * mm});
        }
        {
            var Q0;
            Q0=qCreatedBy(id+"F107.planeOp",FACE);
            var sketch = newSketch(context, id + "F108", { "sketchPlane" : qUnion([Q0])});
            skCircle(sketch, "E139", {"center": v(-126.7, -1303.43) * mm, "radius": 19.05 * mm});
            skCircle(sketch, "E140", {"center": v(-126.7, -1303.43) * mm, "radius": 17.84 * mm});
            skSolve(sketch);
        }
        {
            var Q0;
            Q0 = qSketchRegion(id + "F108", true);
            var Q1;
            Q1=sQuery(id+"F106.wireOp",EDGE,"E136");
            sweep(context, id + "F109", {"operationType" : NewBodyOperationType.ADD, "profiles" : qUnion([Q0]), "path" : qUnion([Q1])});
        }
        {
            var Q0;
            Q0=sQuery(id+"F106.wireOp",VERTEX,"E138.end");
            var Q1;
            Q1=sQuery(id+"F106.wireOp",EDGE,"E138");
            cPlane(context, id + "F110", {"entities" : qUnion([Q0, Q1]), "cplaneType" : CPlaneType.LINE_POINT, "offset" : 25.4 * mm, "width" : 152.4 * mm, "height" : 152.4 * mm});
        }
        {
            var Q0;
            Q0=qCreatedBy(id+"F110.planeOp",FACE);
            var sketch = newSketch(context, id + "F111", { "sketchPlane" : qUnion([Q0])});
            skCircle(sketch, "E141", {"center": v(127.65, -1303.43) * mm, "radius": 19.05 * mm});
            skCircle(sketch, "E142", {"center": v(127.65, -1303.43) * mm, "radius": 17.84 * mm});
            skSolve(sketch);
        }
        {
            var Q0;
            Q0 = qSketchRegion(id + "F111", true);
            var Q1;
            Q1=sQuery(id+"F106.wireOp",EDGE,"E138");
            sweep(context, id + "F112", {"operationType" : NewBodyOperationType.ADD, "profiles" : qUnion([Q0]), "path" : qUnion([Q1])});
        }
        {
            var Q0;
            Q0=sQuery(id+"F106.wireOp",EDGE,"E137");
            cPoint(context, id + "F113", {"entities" : qUnion([Q0]), "parameter" : 0.5});
        }
        {
            var Q0;
            Q0=qCreatedBy(id+"F96.planeOp",FACE);
            var Q1;
            Q1 = qCreatedBy(id + "F113" ,VERTEX);
            cPlane(context, id + "F114", {"entities" : qUnion([Q0, Q1]), "cplaneType" : CPlaneType.PLANE_POINT, "offset" : 25.4 * mm, "width" : 152.4 * mm, "height" : 152.4 * mm});
        }
        {
            var Q0;
            Q0=qCreatedBy(id+"F114.planeOp",FACE);
            var Q1;
            Q1=sQuery(id+"F106.wireOp",EDGE,"E137");
            cPlane(context, id + "F115", {"entities" : qUnion([Q0, Q1]), "cplaneType" : CPlaneType.LINE_ANGLE, "offset" : 25.4 * mm, "angle" : 71 * degree, "width" : 152.4 * mm, "height" : 152.4 * mm});
        }
        {
            var Q0;
            Q0=qCreatedBy(id+"F115.planeOp",FACE);
            var sketch = newSketch(context, id + "F116", { "sketchPlane" : qUnion([Q0])});
            skLineSegment(sketch, "E143", {"start": v(-126.88, -944.4) * mm, "end": v(-291.3, -585.5) * mm});
            skSolve(sketch);
        }
        {
            var Q0;
            Q0=sQuery(id+"F116.wireOp",EDGE,"E143");
            var Q1;
            Q1=sQuery(id+"F116.wireOp",VERTEX,"E143.end");
            cPlane(context, id + "F117", {"entities" : qUnion([Q0, Q1]), "cplaneType" : CPlaneType.LINE_POINT, "offset" : 25.4 * mm, "width" : 152.4 * mm, "height" : 152.4 * mm});
        }
        {
            var Q0;
            Q0=qCreatedBy(id+"F117.planeOp",FACE);
            var sketch = newSketch(context, id + "F118", { "sketchPlane" : qUnion([Q0])});
            skCircle(sketch, "E144", {"center": v(-508.68, 3480.78) * mm, "radius": 19.05 * mm});
            skCircle(sketch, "E145", {"center": v(-508.68, 3480.78) * mm, "radius": 17.84 * mm});
            skSolve(sketch);
        }
        {
            var Q0;
            Q0 = qSketchRegion(id + "F118", true);
            var Q1;
            Q1=sQuery(id+"F116.wireOp",EDGE,"E143");
            sweep(context, id + "F119", {"profiles" : qUnion([Q0]), "path" : qUnion([Q1])});
        }
        {
            var Q0;
            Q0=makeQuery(id+"F119.opSweep","SWEPT_BODY",BODY,{"disambiguationData":[OSD([sQuery(id+"F116.wireOp",EDGE,"E143"),sQuery(id+"F118.wireOp",EDGE,"E144"),sQuery(id+"F118.wireOp",EDGE,"E145")])]});
            var Q1;
            Q1=qCreatedBy(makeId("Right.planeOp"),FACE);
            mirror(context, id + "F120", {"entities" : qUnion([Q0]), "mirrorPlane" : qUnion([Q1])});
        }
        {
            var Q0;
            Q0=qCreatedBy(id+"F61.planeOp",FACE);
            var Q1;
            Q1=makeQuery(id+"F60.opPattern","COPY",FACE,{"derivedFrom":makeQuery(id+"F59.opSweep","SWEPT_FACE",FACE,{"disambiguationData":[OSD([sQuery(id+"F53.wireOp",EDGE,"E93"),sQuery(id+"F58.wireOp",EDGE,"E99")])]}),"instanceName":"1"});
            cPlane(context, id + "F121", {"entities" : qUnion([Q0, Q1]), "cplaneType" : CPlaneType.LINE_ANGLE, "offset" : 25.4 * mm, "angle" : 4 * degree, "width" : 152.4 * mm, "height" : 152.4 * mm});
        }
        {
            var Q0;
            Q0=qCreatedBy(id+"F121.planeOp",FACE);
            var sketch = newSketch(context, id + "F122", { "sketchPlane" : qUnion([Q0])});
            skLineSegment(sketch, "E146", {"start": v(1229.86, 836.71) * mm, "end": v(1256.23, 368.96) * mm});
            skSolve(sketch);
        }
        {
            var Q0;
            Q0=sQuery(id+"F122.wireOp",VERTEX,"E146.start");
            var Q1;
            Q1=sQuery(id+"F122.wireOp",EDGE,"E146");
            cPlane(context, id + "F123", {"entities" : qUnion([Q0, Q1]), "cplaneType" : CPlaneType.LINE_POINT, "offset" : 25.4 * mm, "width" : 152.4 * mm, "height" : 152.4 * mm});
        }
        {
            var Q0;
            Q0=qCreatedBy(id+"F123.planeOp",FACE);
            var sketch = newSketch(context, id + "F124", { "sketchPlane" : qUnion([Q0])});
            skCircle(sketch, "E147", {"center": v(-656.1, -1278.12) * mm, "radius": 19.05 * mm});
            skCircle(sketch, "E148", {"center": v(-656.1, -1278.12) * mm, "radius": 17.84 * mm});
            skSolve(sketch);
        }
        {
            var Q0;
            Q0 = qSketchRegion(id + "F124", true);
            var Q1;
            Q1=sQuery(id+"F122.wireOp",EDGE,"E146");
            sweep(context, id + "F125", {"profiles" : qUnion([Q0]), "path" : qUnion([Q1])});
        }
        {
            var Q0;
            Q0=makeQuery(id+"F125.opSweep","SWEPT_BODY",BODY,{"disambiguationData":[OSD([sQuery(id+"F122.wireOp",EDGE,"E146"),sQuery(id+"F124.wireOp",EDGE,"E147"),sQuery(id+"F124.wireOp",EDGE,"E148")])]});
            var Q1;
            Q1=qCreatedBy(makeId("Right.planeOp"),FACE);
            mirror(context, id + "F126", {"entities" : qUnion([Q0]), "mirrorPlane" : qUnion([Q1])});
        }
        {
            var Q0;
            Q0=qCreatedBy(makeId("Top.planeOp"),FACE);
            var Q1;
            Q1=sQuery(id+"F55.wireOp",VERTEX,"E98.center");
            cPlane(context, id + "F127", {"entities" : qUnion([Q0, Q1]), "cplaneType" : CPlaneType.PLANE_POINT, "offset" : 25.4 * mm, "width" : 152.4 * mm, "height" : 152.4 * mm});
        }
        {
            var Q0;
            Q0=qCreatedBy(id+"F127.planeOp",FACE);
            var Q1;
            Q1=sQuery(id+"F53.wireOp",EDGE,"E92");
            cPlane(context, id + "F128", {"entities" : qUnion([Q0, Q1]), "cplaneType" : CPlaneType.LINE_ANGLE, "offset" : 25.4 * mm, "angle" : 57 * degree, "width" : 152.4 * mm, "height" : 152.4 * mm});
        }
        {
            var Q0;
            Q0=qCreatedBy(id+"F128.planeOp",FACE);
            var sketch = newSketch(context, id + "F129", { "sketchPlane" : qUnion([Q0])});
            skLineSegment(sketch, "E149", {"start": v(-481.62, 1501.72) * mm, "end": v(-469.75, 931.95) * mm});
            skSolve(sketch);
        }
        {
            var Q0;
            Q0=sQuery(id+"F129.wireOp",VERTEX,"E149.start");
            var Q1;
            Q1=sQuery(id+"F129.wireOp",EDGE,"E149");
            cPlane(context, id + "F130", {"entities" : qUnion([Q0, Q1]), "cplaneType" : CPlaneType.LINE_POINT, "offset" : 25.4 * mm, "width" : 152.4 * mm, "height" : 152.4 * mm});
        }
        {
            var Q0;
            Q0=qCreatedBy(id+"F130.planeOp",FACE);
            var sketch = newSketch(context, id + "F131", { "sketchPlane" : qUnion([Q0])});
            skCircle(sketch, "E150", {"center": v(450.24, -505.96) * mm, "radius": 19.05 * mm});
            skCircle(sketch, "E151", {"center": v(450.24, -505.96) * mm, "radius": 17.84 * mm});
            skSolve(sketch);
        }
        {
            var Q0;
            Q0 = qSketchRegion(id + "F131", true);
            var Q1;
            Q1=sQuery(id+"F129.wireOp",EDGE,"E149");
            sweep(context, id + "F132", {"profiles" : qUnion([Q0]), "path" : qUnion([Q1])});
        }
        {
            var Q0;
            Q0=makeQuery(id+"F132.opSweep","SWEPT_BODY",BODY,{"disambiguationData":[OSD([sQuery(id+"F129.wireOp",EDGE,"E149"),sQuery(id+"F131.wireOp",EDGE,"E150"),sQuery(id+"F131.wireOp",EDGE,"E151")])]});
            var Q1;
            Q1=qCreatedBy(makeId("Right.planeOp"),FACE);
            mirror(context, id + "F133", {"entities" : qUnion([Q0]), "mirrorPlane" : qUnion([Q1])});
        }
        {
            var Q0;
            Q0=qCreatedBy(id+"F127.planeOp",FACE);
            var Q1;
            Q1=sQuery(id+"F53.wireOp",VERTEX,"E94.end");
            cPlane(context, id + "F134", {"entities" : qUnion([Q0, Q1]), "cplaneType" : CPlaneType.PLANE_POINT, "offset" : 25.4 * mm, "width" : 152.4 * mm, "height" : 152.4 * mm});
        }
        {
            var Q0;
            Q0=qCreatedBy(id+"F134.planeOp",FACE);
            var Q1;
            Q1=sQuery(id+"F53.wireOp",EDGE,"E94");
            cPlane(context, id + "F135", {"entities" : qUnion([Q0, Q1]), "cplaneType" : CPlaneType.LINE_ANGLE, "offset" : 25.4 * mm, "angle" : 147 * degree, "oppositeDirection" : true, "width" : 152.4 * mm, "height" : 152.4 * mm});
        }
        {
            var Q0;
            Q0=qCreatedBy(id+"F135.planeOp",FACE);
            var sketch = newSketch(context, id + "F136", { "sketchPlane" : qUnion([Q0])});
            skLineSegment(sketch, "E152", {"start": v(482.96, 1167.5) * mm, "end": v(290.7, 1916.37) * mm});
            skSolve(sketch);
        }
        {
            var Q0;
            Q0=sQuery(id+"F136.wireOp",EDGE,"E152");
            var Q1;
            Q1=sQuery(id+"F136.wireOp",VERTEX,"E152.start");
            cPlane(context, id + "F137", {"entities" : qUnion([Q0, Q1]), "cplaneType" : CPlaneType.LINE_POINT, "offset" : 25.4 * mm, "width" : 152.4 * mm, "height" : 152.4 * mm});
        }
        {
            var Q0;
            Q0=qCreatedBy(id+"F137.planeOp",FACE);
            var sketch = newSketch(context, id + "F138", { "sketchPlane" : qUnion([Q0])});
            skCircle(sketch, "E153", {"center": v(-758.12, 1933.84) * mm, "radius": 19.05 * mm});
            skCircle(sketch, "E154", {"center": v(-758.12, 1933.84) * mm, "radius": 17.84 * mm});
            skSolve(sketch);
        }
        {
            var Q0;
            Q0 = qSketchRegion(id + "F138", true);
            var Q1;
            Q1=sQuery(id+"F136.wireOp",EDGE,"E152");
            sweep(context, id + "F139", {"profiles" : qUnion([Q0]), "path" : qUnion([Q1])});
        }
        {
            var Q0;
            Q0=makeQuery(id+"F139.opSweep","SWEPT_BODY",BODY,{"disambiguationData":[OSD([sQuery(id+"F136.wireOp",EDGE,"E152"),sQuery(id+"F138.wireOp",EDGE,"E153"),sQuery(id+"F138.wireOp",EDGE,"E154")])]});
            var Q1;
            Q1=qCreatedBy(makeId("Right.planeOp"),FACE);
            mirror(context, id + "F140", {"entities" : qUnion([Q0]), "mirrorPlane" : qUnion([Q1])});
        }
    });
